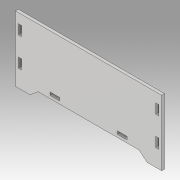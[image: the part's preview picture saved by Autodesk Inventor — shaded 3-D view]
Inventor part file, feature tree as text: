
AUTODESK INVENTOR PART (.ipt)
format: ipt  version: 2019.3 (Build 233278000, 278)  size: 125,440 bytes
history: native  units: mm
features: extrude x1, sketch x1
ambient origin geometry x8: Origin, YZ Plane, XZ Plane, XY Plane, X Axis, Y Axis, Z Axis, Center Point
bodies: Solid1 (feature_tree)
feature tree (2):
  extrude  "Extrusion1"  Depth=10.0mm
  sketch  "Sketch1"  dims[d0=3.0mm d1=10.0mm d2=60.0mm d3=10.0mm d4=152.0mm d5=36.0mm d6=36.0mm d7=3.1mm d8=10.0mm d9=20.0mm d10=5.0mm d11=10.0mm d12=3.0mm d13=3.0mm d14=3.0mm d15=15.0mm d16=15.0mm d17=105.0mm d18=3.0mm d19=0.0mm]
